# Revit family: Shower-Valve_Trim-KOHLER-PURIST-C14490W_1
name_source: partatom
category: Plumbing Fixtures
revit_build: Autodesk Revit 2017 (Build: 20160225_1515(x64)
units: mm (PartAtom-declared; Revit-internal decimal feet)

## family parameters
Cut with Voids When Loaded = No
Host = Face
OmniClass Number = 23.31.17.00
OmniClass Title = Showers
Part Type = Normal
Room Calculation Point = No
Round Connector Dimension = Use Diameter
Shared = No

## types (2) — shared parameters
ADA Compliant = No
Assembly Code = D2010700
CW Connection = No
Cold Water Inlet = Cold Water Inlet
Date Modified = 07/20/2021
Default Elevation = 42"
Drain Included = No
Finish = Kohler-Metal-CP-Polished_Chrome
Flow Rate = 0 GPM
HW Connection = Yes
Height = 3 7/8"
Length = 4 3/16"
Manufacturer = KOHLER Co.
Master Format 2014 = 22 42 23
Master Format 2014 Name = Residential Showers
Material = Premium Metal Construction
Pressure = 0.00 psi
Product Name = PURIST
Tempered Water Inlet = Tempered Water Inlet
Tempered Water Outlet = Tempered Water Outlet
URL = https://www.kohler.co.uk
Vent Connection = No
Waste Connection = No
Waste Water Outlet = Waste Water Outlet
WaterSense Certified = No
Width = 3 7/8"

## per-type parameters (varying)
| type | Cross Handle | Description | Handle Clearance | Lever Handle | Model | Type |
| Cross Handle, CP-Polished Chrome | Yes | Flow Control Valve, Cross Handle | 1 3/4" | No | C14490W-3-CP | 1 |
| Lever Handle, CP-Polished Chrome | No | Lever Flow Control Valve & Trim | 2 5/8" | Yes | C14490W-4-CP | 2 |

## geometry (parser evidence)
native form markers: Sweep x4
no freeform markers — native parametric forms only
